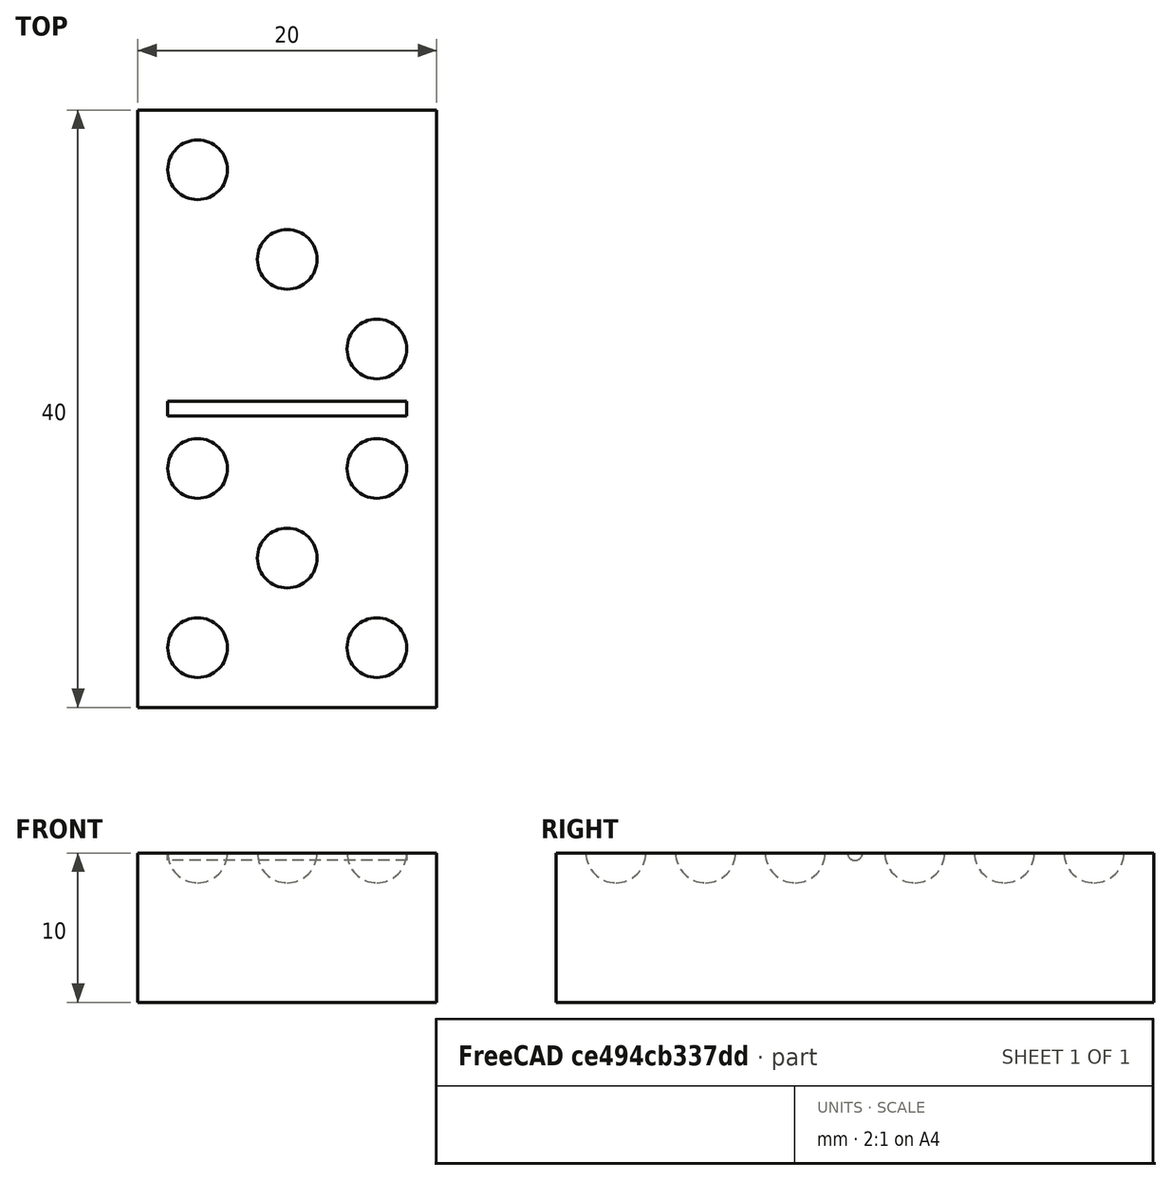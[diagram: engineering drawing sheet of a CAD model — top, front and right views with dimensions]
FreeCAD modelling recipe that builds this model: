
FCSTD DOCUMENT  (FreeCAD 0.21R33694 (Git))
Label: OJT1_T13P04.domino
License: All rights reserved
LicenseURL: http://en.wikipedia.org/wiki/All_rights_reserved
objects: Part::Cut×9, Part::Sphere×8, Part::Box×1, Part::Cylinder×1
note: 19 computed .brp shape members not serialized (recipe doc carries the construction recipe); baked Part::Feature solids carry a one-line shape summary decoded from their .brp

FEATURE [Part::Box] Box  label="Cub"
  AttacherType = Attacher::AttachEngine3D
  Height = 10
  Length = 20
  Width = 40
FEATURE [Part::Sphere] Sphere  label="Esfera"
  Angle1 = -90
  Angle2 = 90
  Angle3 = 360
  AttacherType = Attacher::AttachEngine3D
  Placement = pos=(4,4,10) rot=(0,0,1;0rad)
  Radius = 2
FEATURE [Part::Sphere] Sphere001  label="Esfera001"
  Angle1 = -90
  Angle2 = 90
  Angle3 = 360
  AttacherType = Attacher::AttachEngine3D
  Placement = pos=(16,4,10) rot=(0,0,1;0rad)
  Radius = 2
FEATURE [Part::Sphere] Sphere002  label="Esfera002"
  Angle1 = -90
  Angle2 = 90
  Angle3 = 360
  AttacherType = Attacher::AttachEngine3D
  Placement = pos=(10,10,10) rot=(0,0,1;0rad)
  Radius = 2
FEATURE [Part::Sphere] Sphere003  label="Esfera003"
  Angle1 = -90
  Angle2 = 90
  Angle3 = 360
  AttacherType = Attacher::AttachEngine3D
  Placement = pos=(4,16,10) rot=(0,0,1;0rad)
  Radius = 2
FEATURE [Part::Sphere] Sphere004  label="Esfera004"
  Angle1 = -90
  Angle2 = 90
  Angle3 = 360
  AttacherType = Attacher::AttachEngine3D
  Placement = pos=(16,16,10) rot=(0,0,1;0rad)
  Radius = 2
FEATURE [Part::Sphere] Sphere005  label="Esfera005"
  Angle1 = -90
  Angle2 = 90
  Angle3 = 360
  AttacherType = Attacher::AttachEngine3D
  Placement = pos=(4,36,10) rot=(0,0,1;0rad)
  Radius = 2
FEATURE [Part::Sphere] Sphere006  label="Esfera006"
  Angle1 = -90
  Angle2 = 90
  Angle3 = 360
  AttacherType = Attacher::AttachEngine3D
  Placement = pos=(10,30,10) rot=(0,0,1;0rad)
  Radius = 2
FEATURE [Part::Sphere] Sphere007  label="Esfera007"
  Angle1 = -90
  Angle2 = 90
  Angle3 = 360
  AttacherType = Attacher::AttachEngine3D
  Placement = pos=(16,24,10) rot=(0,0,1;0rad)
  Radius = 2
FEATURE [Part::Cylinder] Cylinder  label="Cilindre"
  Angle = 360
  AttacherType = Attacher::AttachEngine3D
  FirstAngle = 0
  Height = 16
  Placement = pos=(2,20,10) rot=(0,1,0;1.5708rad)
  Radius = 0.5
  SecondAngle = 0
FEATURE [Part::Cut] Cut
  Base = -> Box
  Refine = true
  Tool = -> Sphere005
FEATURE [Part::Cut] Cut001
  Base = -> Cut
  Refine = true
  Tool = -> Sphere006
FEATURE [Part::Cut] Cut002
  Base = -> Cut001
  Refine = true
  Tool = -> Sphere007
FEATURE [Part::Cut] Cut003
  Base = -> Cut002
  Refine = true
  Tool = -> Cylinder
FEATURE [Part::Cut] Cut004
  Base = -> Cut003
  Refine = true
  Tool = -> Sphere004
FEATURE [Part::Cut] Cut005
  Base = -> Cut004
  Refine = true
  Tool = -> Sphere003
FEATURE [Part::Cut] Cut006
  Base = -> Cut005
  Refine = true
  Tool = -> Sphere002
FEATURE [Part::Cut] Cut007
  Base = -> Cut006
  Refine = true
  Tool = -> Sphere001
FEATURE [Part::Cut] Cut008
  Base = -> Cut007
  Refine = true
  Tool = -> Sphere
